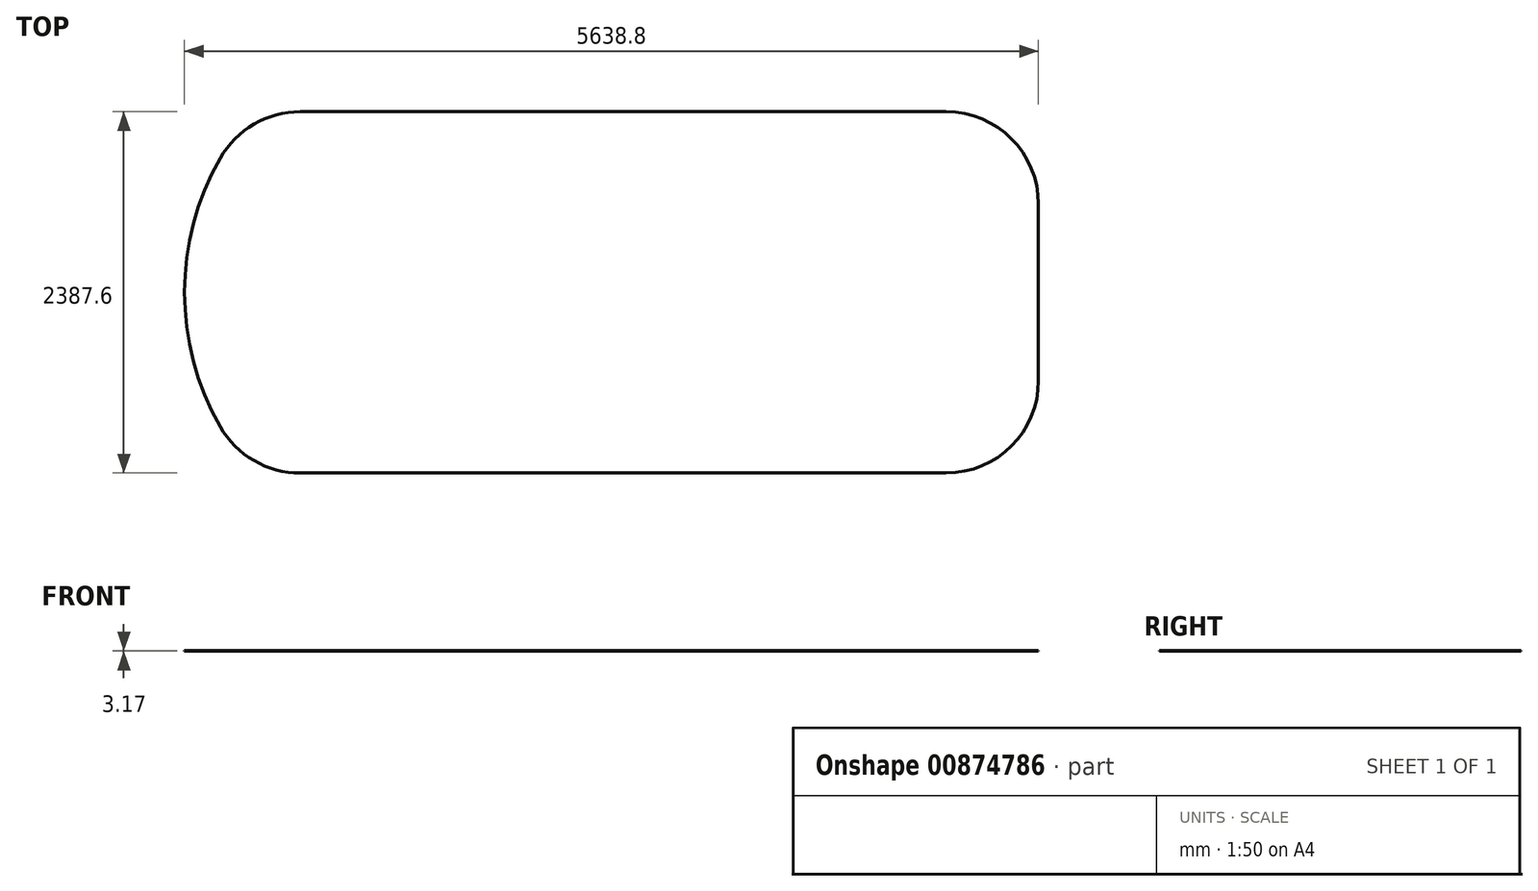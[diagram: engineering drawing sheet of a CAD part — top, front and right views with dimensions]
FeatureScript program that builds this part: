
annotation { "Feature Type Name" : "Feature", "Feature Type Description" : "" }
export const myFeature = defineFeature(function(context is Context, id is Id, definition is map)
    precondition{}
    {
        {
            var Q0;
            Q0=qCreatedBy(makeId("Top.planeOp"),FACE);
            var sketch = newSketch(context, id + "F0", { "sketchPlane" : qUnion([Q0])});
            skLineSegment(sketch, "E0.bottom", {"start": v(-2283.27, 1193.8) * mm, "end": v(1981.2, 1193.8) * mm});
            skLineSegment(sketch, "E0.top", {"start": v(-2283.27, -1193.8) * mm, "end": v(1981.2, -1193.8) * mm});
            skLineSegment(sketch, "E0.left", {"start": v(-2590.8, 1193.8) * mm, "end": v(-2590.8, -1193.8) * mm});
            skLineSegment(sketch, "E0.right", {"start": v(2590.8, 584.2) * mm, "end": v(2590.8, -584.2) * mm});
            skPoint(sketch, "E0.middle", {"position": v(0, 0) * mm});
            skPoint(sketch, "E1.visualSharp", {"position": v(2590.8, 1193.8) * mm});
            skArc(sketch, "E1.filletArc", {"start": v(2590.8, 584.2) * mm, "mid": v(2412.25, 1015.25) * mm, "end": v(1981.2, 1193.8) * mm});
            skPoint(sketch, "E2.visualSharp", {"position": v(2590.8, -1193.8) * mm});
            skArc(sketch, "E2.filletArc", {"start": v(1981.2, -1193.8) * mm, "mid": v(2412.25, -1015.25) * mm, "end": v(2590.8, -584.2) * mm});
            skLineSegment(sketch, "E3", {"start": v(2590.8, 584.2) * mm, "end": v(2590.8, -584.2) * mm, "construction": true});
            skLineSegment(sketch, "E4", {"start": v(-2590.8, 0) * mm, "end": v(-3048, 0) * mm, "construction": true});
            skLineSegment(sketch, "E5", {"start": v(-2590.8, 1193.8) * mm, "end": v(-3048, 1193.8) * mm, "construction": true});
            skPoint(sketch, "E6.1.internal.snap0", {"position": v(-2819.4, 1193.8) * mm});
            skPoint(sketch, "E6.5.internal.snap0", {"position": v(-2819.4, 1193.8) * mm});
            skArc(sketch, "E7", {"start": v(-2812.56, 886.63) * mm, "mid": v(-3048, 0) * mm, "end": v(-2812.56, -886.63) * mm});
            skPoint(sketch, "E8.visualSharp", {"position": v(-2590.8, 1193.8) * mm});
            skArc(sketch, "E8.filletArc", {"start": v(-2283.27, 1193.8) * mm, "mid": v(-2589.25, 1111.44) * mm, "end": v(-2812.56, 886.63) * mm});
            skPoint(sketch, "E9.visualSharp", {"position": v(-2590.8, -1193.8) * mm});
            skArc(sketch, "E9.filletArc", {"start": v(-2812.56, -886.63) * mm, "mid": v(-2589.25, -1111.44) * mm, "end": v(-2283.27, -1193.8) * mm});
            skLineSegment(sketch, "E10", {"start": v(-2283.27, 1193.8) * mm, "end": v(0, 1193.8) * mm, "construction": true});
            skLineSegment(sketch, "E11", {"start": v(-2283.27, 1193.8) * mm, "end": v(-2283.27, -1193.8) * mm, "construction": true});
            skText(sketch, "E12", { "text": "front\n", "fontName": "OpenSans-Regular.ttf"});
            const initialGuessF0  = {"E12": [-4.48252, 0.01492, 1, 0, 0.22806]};
            skSetInitialGuess(sketch, initialGuessF0);
            skSolve(sketch);
        }
        {
            var Q0;
            {var subQ6=sQuery(id+"F0.wireOp",EDGE,"E0.bottom");Q0=makeQuery(id+"F0.imprint","IMPRINT",FACE,{"disambiguationData":[TD([[makeQuery(id+"F0.imprint","IMPRINT",EDGE,{"derivedFrom":subQ6}),-1.0]])]});}
            var Q1;
            {var subQ5=sQuery(id+"F0.wireOp",EDGE,"E7");Q1=makeQuery(id+"F0.imprint","IMPRINT",FACE,{"disambiguationData":[TD([[makeQuery(id+"F0.imprint","IMPRINT",EDGE,{"derivedFrom":subQ5}),1.0]])]});}
            extrude(context, id + "F1", {"entities" : qUnion([Q0, Q1]), "depth" : 3.17 * mm, "offsetDistance" : 25.4 * mm});
        }
    });
